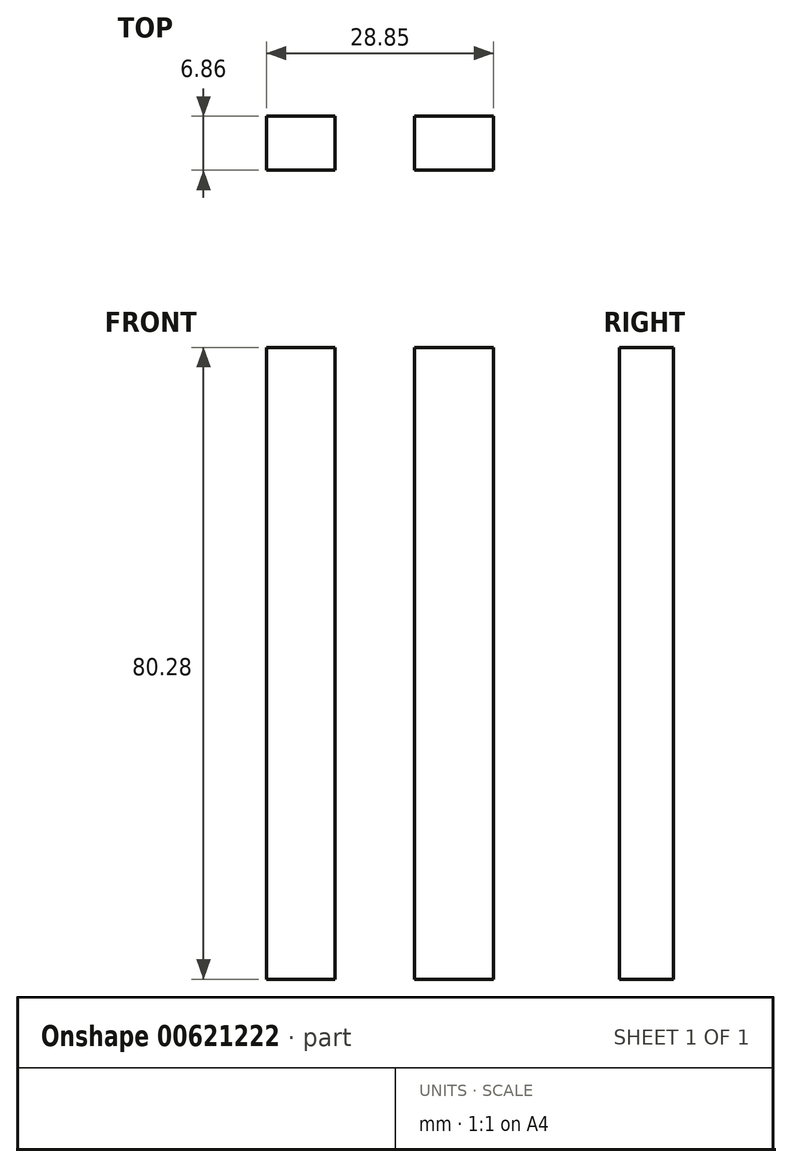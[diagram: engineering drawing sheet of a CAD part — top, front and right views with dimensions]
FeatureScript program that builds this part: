
annotation { "Feature Type Name" : "Feature", "Feature Type Description" : "" }
export const myFeature = defineFeature(function(context is Context, id is Id, definition is map)
    precondition{}
    {
        {
            var Q0;
            Q0=qCreatedBy(makeId("Front.planeOp"),FACE);
            var sketch = newSketch(context, id + "F0", { "sketchPlane" : qUnion([Q0])});
            skLineSegment(sketch, "E0.bottom", {"start": v(-47.76, 48.03) * mm, "end": v(-39.05, 48.03) * mm});
            skLineSegment(sketch, "E0.top", {"start": v(-47.76, -32.25) * mm, "end": v(-39.05, -32.25) * mm});
            skLineSegment(sketch, "E0.left", {"start": v(-47.76, 48.03) * mm, "end": v(-47.76, -32.25) * mm});
            skLineSegment(sketch, "E0.right", {"start": v(-39.05, 48.03) * mm, "end": v(-39.05, -32.25) * mm});
            skLineSegment(sketch, "E1.bottom", {"start": v(-28.98, 48.03) * mm, "end": v(-18.91, 48.03) * mm});
            skLineSegment(sketch, "E1.top", {"start": v(-28.98, -32.25) * mm, "end": v(-18.91, -32.25) * mm});
            skLineSegment(sketch, "E1.left", {"start": v(-28.98, 48.03) * mm, "end": v(-28.98, -32.25) * mm});
            skLineSegment(sketch, "E1.right", {"start": v(-18.91, 48.03) * mm, "end": v(-18.91, -32.25) * mm});
            skSolve(sketch);
        }
        {
            var Q0;
            Q0 = qSketchRegion(id + "F0", true);
            extrude(context, id + "F1", {"entities" : qUnion([Q0]), "depth" : 6.86 * mm, "offsetDistance" : 25.4 * mm});
        }
    });
